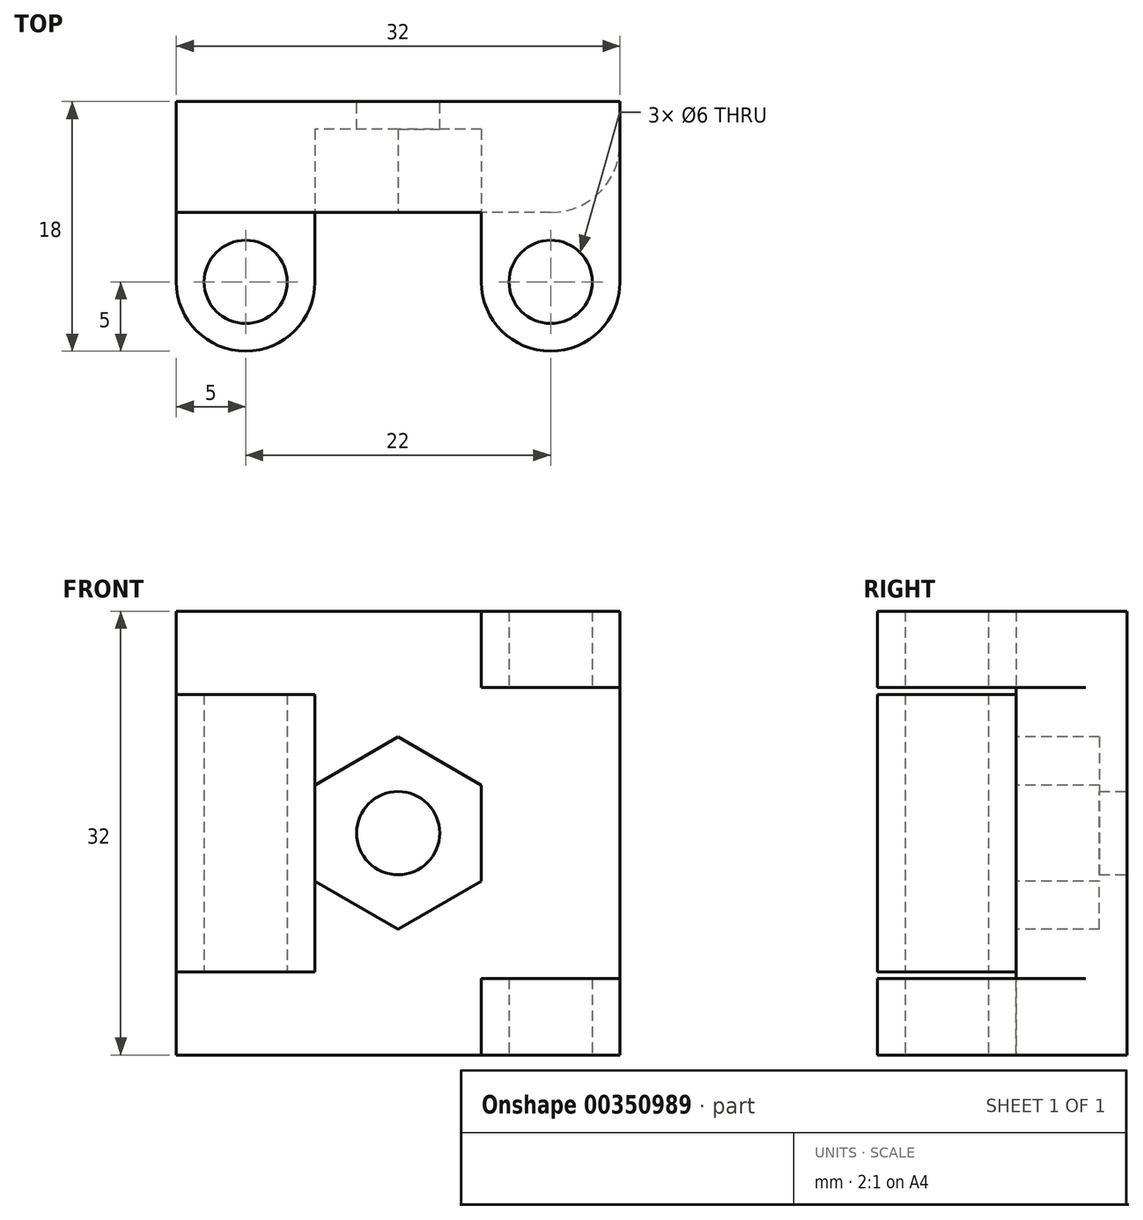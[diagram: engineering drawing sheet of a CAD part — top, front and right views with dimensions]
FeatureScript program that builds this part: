
annotation { "Feature Type Name" : "Feature", "Feature Type Description" : "" }
export const myFeature = defineFeature(function(context is Context, id is Id, definition is map)
    precondition{}
    {
        {
            var Q0;
            Q0=qCreatedBy(makeId("Front.planeOp"),FACE);
            var sketch = newSketch(context, id + "F0", { "sketchPlane" : qUnion([Q0])});
            skLineSegment(sketch, "E0.bottom", {"start": v(-16, 16) * mm, "end": v(16, 16) * mm});
            skLineSegment(sketch, "E0.top", {"start": v(-16, -16) * mm, "end": v(16, -16) * mm});
            skLineSegment(sketch, "E0.left", {"start": v(-16, 16) * mm, "end": v(-16, -16) * mm});
            skLineSegment(sketch, "E0.right", {"start": v(16, 16) * mm, "end": v(16, -16) * mm});
            skLineSegment(sketch, "E1", {"start": v(-16, 16) * mm, "end": v(16, -16) * mm, "construction": true});
            skSolve(sketch);
        }
        {
            var Q0;
            Q0 = qSketchRegion(id + "F0", true);
            extrude(context, id + "F1", {"entities" : qUnion([Q0]), "depth" : 8 * mm});
        }
        {
            var Q0;
            Q0=makeQuery(id+"F1.opExtrude","CAP_FACE",FACE,{"disambiguationData":[OSD([sQuery(id+"F0.wireOp",EDGE,"E0.bottom"),sQuery(id+"F0.wireOp",EDGE,"E0.top"),sQuery(id+"F0.wireOp",EDGE,"E0.left"),sQuery(id+"F0.wireOp",EDGE,"E0.right")])],"isStart":false});
            var sketch = newSketch(context, id + "F2", { "sketchPlane" : qUnion([Q0])});
            skLineSegment(sketch, "E2.left", {"start": v(-16, 10) * mm, "end": v(-16, -10) * mm});
            skLineSegment(sketch, "E2.right", {"start": v(-6, 10) * mm, "end": v(-6, -10) * mm});
            skLineSegment(sketch, "E3.bottom", {"start": v(-16, 10) * mm, "end": v(-6, 10) * mm});
            skLineSegment(sketch, "E3.top", {"start": v(-16, -10) * mm, "end": v(-6, -10) * mm});
            skLineSegment(sketch, "E4.bottom", {"start": v(16, -16) * mm, "end": v(6, -16) * mm});
            skLineSegment(sketch, "E4.top", {"start": v(16, -10.5) * mm, "end": v(6, -10.5) * mm});
            skLineSegment(sketch, "E4.left", {"start": v(16, -16) * mm, "end": v(16, -10.5) * mm});
            skLineSegment(sketch, "E4.right", {"start": v(6, -16) * mm, "end": v(6, -10.5) * mm});
            skLineSegment(sketch, "E5.bottom", {"start": v(16, 16) * mm, "end": v(6, 16) * mm});
            skLineSegment(sketch, "E5.top", {"start": v(16, 10.5) * mm, "end": v(6, 10.5) * mm});
            skLineSegment(sketch, "E5.left", {"start": v(16, 16) * mm, "end": v(16, 10.5) * mm});
            skLineSegment(sketch, "E5.right", {"start": v(6, 16) * mm, "end": v(6, 10.5) * mm});
            skSolve(sketch);
        }
        {
            var Q0;
            Q0 = qSketchRegion(id + "F2", true);
            extrude(context, id + "F3", {"entities" : qUnion([Q0]), "operationType" : NewBodyOperationType.ADD, "depth" : 10 * mm});
        }
        {
            var Q0;
            Q0=makeQuery(id+"F1.opExtrude","CAP_FACE",FACE,{"disambiguationData":[OSD([sQuery(id+"F0.wireOp",EDGE,"E0.bottom"),sQuery(id+"F0.wireOp",EDGE,"E0.top"),sQuery(id+"F0.wireOp",EDGE,"E0.left"),sQuery(id+"F0.wireOp",EDGE,"E0.right")])],"isStart":false});
            var sketch = newSketch(context, id + "F4", { "sketchPlane" : qUnion([Q0])});
            skCircle(sketch, "E6.cCircle", {"center": v(0, 0) * mm, "radius": 6 * mm, "construction": true});
            skLineSegment(sketch, "E6.0", {"start": v(6, 3.46) * mm, "end": v(6, -3.46) * mm});
            skLineSegment(sketch, "E6.1", {"start": v(6, -3.46) * mm, "end": v(0, -6.93) * mm});
            skLineSegment(sketch, "E6.2", {"start": v(0, -6.93) * mm, "end": v(-6, -3.46) * mm});
            skLineSegment(sketch, "E6.3", {"start": v(-6, -3.46) * mm, "end": v(-6, 3.46) * mm});
            skLineSegment(sketch, "E6.4", {"start": v(-6, 3.46) * mm, "end": v(0, 6.93) * mm});
            skLineSegment(sketch, "E6.5", {"start": v(0, 6.93) * mm, "end": v(6, 3.46) * mm});
            skPoint(sketch, "E6.0.midPoint", {"position": v(6, 0) * mm});
            skSolve(sketch);
        }
        {
            var Q0;
            Q0 = qSketchRegion(id + "F4", true);
            extrude(context, id + "F5", {"entities" : qUnion([Q0]), "operationType" : NewBodyOperationType.REMOVE, "oppositeDirection" : true, "depth" : 6 * mm});
        }
        {
            var Q0;
            Q0=makeQuery(id+"F1.opExtrude","CAP_FACE",FACE,{"disambiguationData":[OSD([sQuery(id+"F0.wireOp",EDGE,"E0.bottom"),sQuery(id+"F0.wireOp",EDGE,"E0.top"),sQuery(id+"F0.wireOp",EDGE,"E0.left"),sQuery(id+"F0.wireOp",EDGE,"E0.right")])],"isStart":true});
            var sketch = newSketch(context, id + "F6", { "sketchPlane" : qUnion([Q0])});
            skCircle(sketch, "E7", {"center": v(0, 0) * mm, "radius": 3 * mm});
            skSolve(sketch);
        }
        {
            var Q0;
            Q0 = qSketchRegion(id + "F6", true);
            extrude(context, id + "F7", {"entities" : qUnion([Q0]), "operationType" : NewBodyOperationType.REMOVE, "oppositeDirection" : true, "depth" : 25 * mm});
        }
        {
            var Q0;
            Q0=makeQuery(id+"F3.opExtrude","SWEPT_FACE",FACE,{"disambiguationData":[OSD([sQuery(id+"F2.wireOp",EDGE,"E3.top")])]});
            var sketch = newSketch(context, id + "F8", { "sketchPlane" : qUnion([Q0])});
            skLineSegment(sketch, "E8", {"start": v(-16, 8) * mm, "end": v(-6, 18) * mm, "construction": true});
            skCircle(sketch, "E9", {"center": v(-11, 13) * mm, "radius": 3 * mm});
            skSolve(sketch);
        }
        {
            var Q0;
            Q0 = qSketchRegion(id + "F8", true);
            extrude(context, id + "F9", {"entities" : qUnion([Q0]), "operationType" : NewBodyOperationType.REMOVE, "oppositeDirection" : true, "depth" : 25 * mm});
        }
        {
            var Q0;
            Q0=makeQuery(id+"F3.boolean.opBoolean","MERGE",FACE,{"derivedFrom":[makeQuery(id+"F1.opExtrude","SWEPT_FACE",FACE,{"disambiguationData":[OSD([sQuery(id+"F0.wireOp",EDGE,"E0.top")])]}),makeQuery(id+"F3.opExtrude","SWEPT_FACE",FACE,{"disambiguationData":[OSD([sQuery(id+"F2.wireOp",EDGE,"E4.bottom")])]})]});
            var sketch = newSketch(context, id + "F10", { "sketchPlane" : qUnion([Q0])});
            skLineSegment(sketch, "E10", {"start": v(6, 8) * mm, "end": v(16, 18) * mm, "construction": true});
            skCircle(sketch, "E11", {"center": v(11, 13) * mm, "radius": 3 * mm});
            skSolve(sketch);
        }
        {
            var Q0;
            Q0 = qSketchRegion(id + "F10", true);
            extrude(context, id + "F11", {"entities" : qUnion([Q0]), "operationType" : NewBodyOperationType.REMOVE, "endBound" : BoundingType.THROUGH_ALL, "oppositeDirection" : true, "depth" : 25 * mm});
        }
        {
            var Q0;
            Q0=makeQuery(id+"F3.opExtrude","CAP_EDGE",EDGE,{"disambiguationData":[OSD([sQuery(id+"F2.wireOp",EDGE,"E5.right")])],"isStart":false});
            var Q1;
            Q1=makeQuery(id+"F3.opExtrude","CAP_EDGE",EDGE,{"disambiguationData":[OSD([sQuery(id+"F2.wireOp",EDGE,"E5.left")])],"isStart":false});
            var Q2;
            Q2=makeQuery(id+"F3.opExtrude","CAP_EDGE",EDGE,{"disambiguationData":[OSD([sQuery(id+"F2.wireOp",EDGE,"E4.left")])],"isStart":false});
            var Q3;
            Q3=makeQuery(id+"F3.opExtrude","CAP_EDGE",EDGE,{"disambiguationData":[OSD([sQuery(id+"F2.wireOp",EDGE,"E4.right")])],"isStart":false});
            fillet(context, id + "F12", {"entities" : qUnion([Q0, Q1, Q2, Q3]), "radius" : 5 * mm, "tangentPropagation" : true, "allowEdgeOverflow" : false});
        }
        {
            var Q0;
            Q0=makeQuery(id+"F3.opExtrude","CAP_EDGE",EDGE,{"disambiguationData":[OSD([sQuery(id+"F2.wireOp",EDGE,"E2.right")])],"isStart":false});
            var Q1;
            Q1=makeQuery(id+"F3.opExtrude","CAP_EDGE",EDGE,{"disambiguationData":[OSD([sQuery(id+"F2.wireOp",EDGE,"E2.left")])],"isStart":false});
            fillet(context, id + "F13", {"entities" : qUnion([Q0, Q1]), "radius" : 5 * mm, "tangentPropagation" : true, "allowEdgeOverflow" : false});
        }
        {
            var Q0;
            Q0=makeQuery(id+"F1.opExtrude","CAP_EDGE",EDGE,{"disambiguationData":[OSD([sQuery(id+"F0.wireOp",EDGE,"E0.right")])],"isStart":false});
            fillet(context, id + "F14", {"entities" : qUnion([Q0]), "radius" : 5 * mm, "tangentPropagation" : true, "allowEdgeOverflow" : false});
        }
    });
